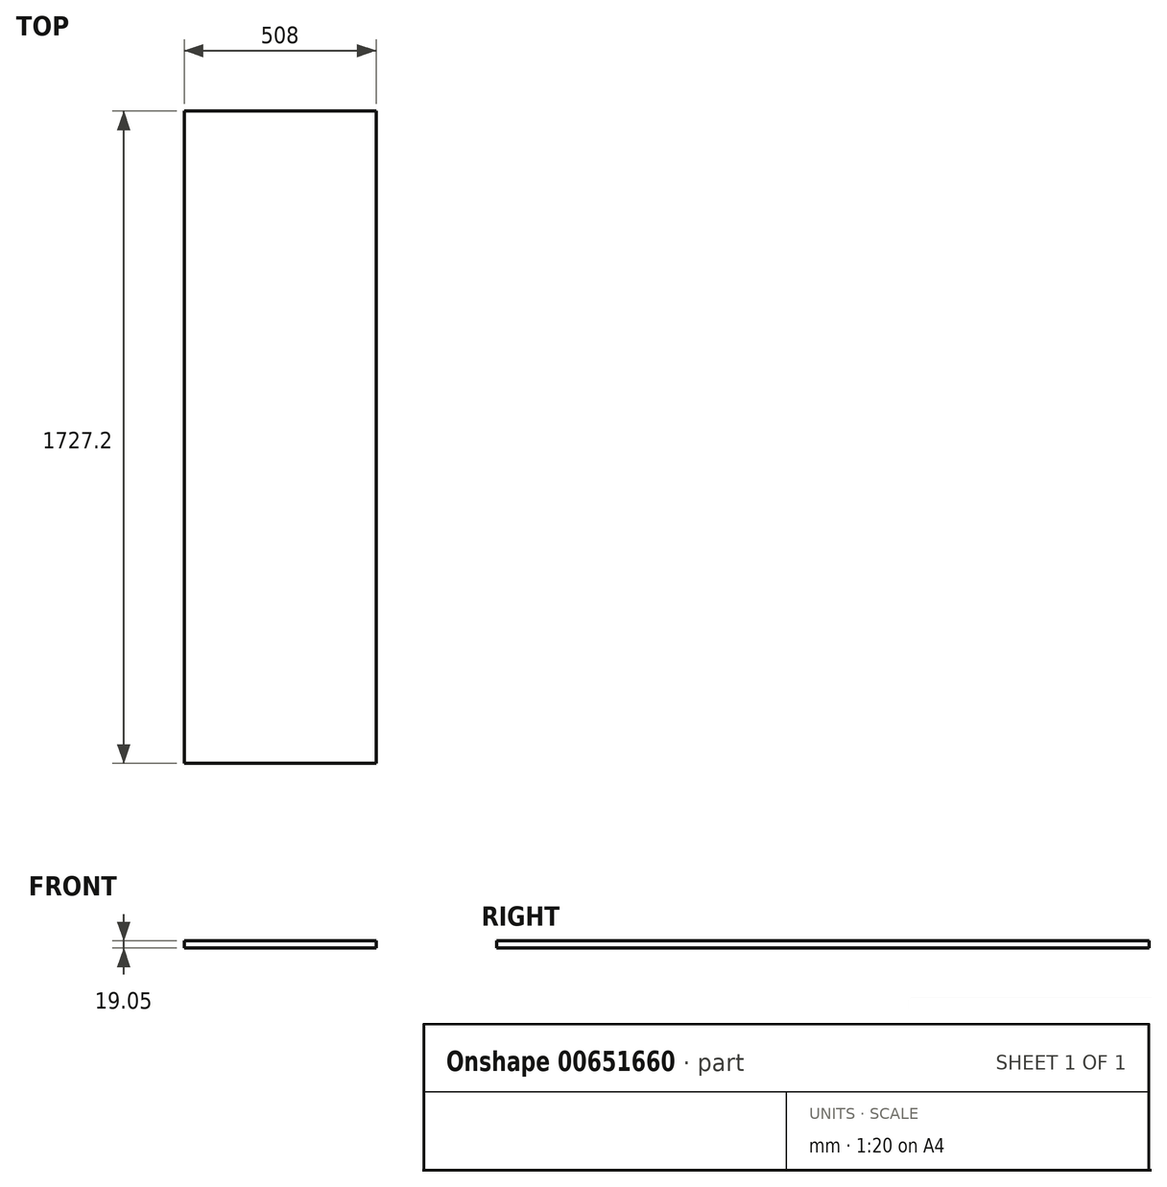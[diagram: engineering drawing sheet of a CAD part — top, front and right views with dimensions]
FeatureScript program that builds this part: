
annotation { "Feature Type Name" : "Feature", "Feature Type Description" : "" }
export const myFeature = defineFeature(function(context is Context, id is Id, definition is map)
    precondition{}
    {
        {
            var Q0;
            Q0=qCreatedBy(makeId("Top.planeOp"),FACE);
            var sketch = newSketch(context, id + "F0", { "sketchPlane" : qUnion([Q0])});
            skLineSegment(sketch, "E0.bottom", {"start": v(-255.05, 1577.26) * mm, "end": v(252.95, 1577.26) * mm});
            skLineSegment(sketch, "E0.top", {"start": v(-255.05, -149.94) * mm, "end": v(252.95, -149.94) * mm});
            skLineSegment(sketch, "E0.left", {"start": v(-255.05, 1577.26) * mm, "end": v(-255.05, -149.94) * mm});
            skLineSegment(sketch, "E0.right", {"start": v(252.95, 1577.26) * mm, "end": v(252.95, -149.94) * mm});
            skSolve(sketch);
        }
        {
            var Q0;
            Q0 = qSketchRegion(id + "F0", true);
            extrude(context, id + "F1", {"entities" : qUnion([Q0]), "depth" : 19.05 * mm, "offsetDistance" : 25.4 * mm});
        }
    });
